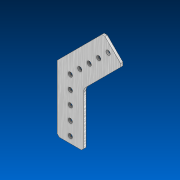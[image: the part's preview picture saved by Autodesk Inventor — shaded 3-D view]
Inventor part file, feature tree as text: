
AUTODESK INVENTOR PART (.ipt)
format: ipt  version: 2022.2 (Build 262287000, 287)  size: 111,616 bytes
history: native  units: in
note: dims shown in document units (in); Inventor stores cm internally (conversion verified against a paired STEP export)
features: fillet x1
ambient origin geometry x8: Origin, YZ Plane, XZ Plane, XY Plane, X Axis, Y Axis, Z Axis, Center Point
bodies: Solid1 (feature_tree)
feature tree (1):
  fillet  "Fillet2"  [1 undecoded]
note: 1 required parameter value undecoded (feature->parameter linkage not recoverable at this tier; creation-order binding heuristic only, values carry confidence <= 0.55)
